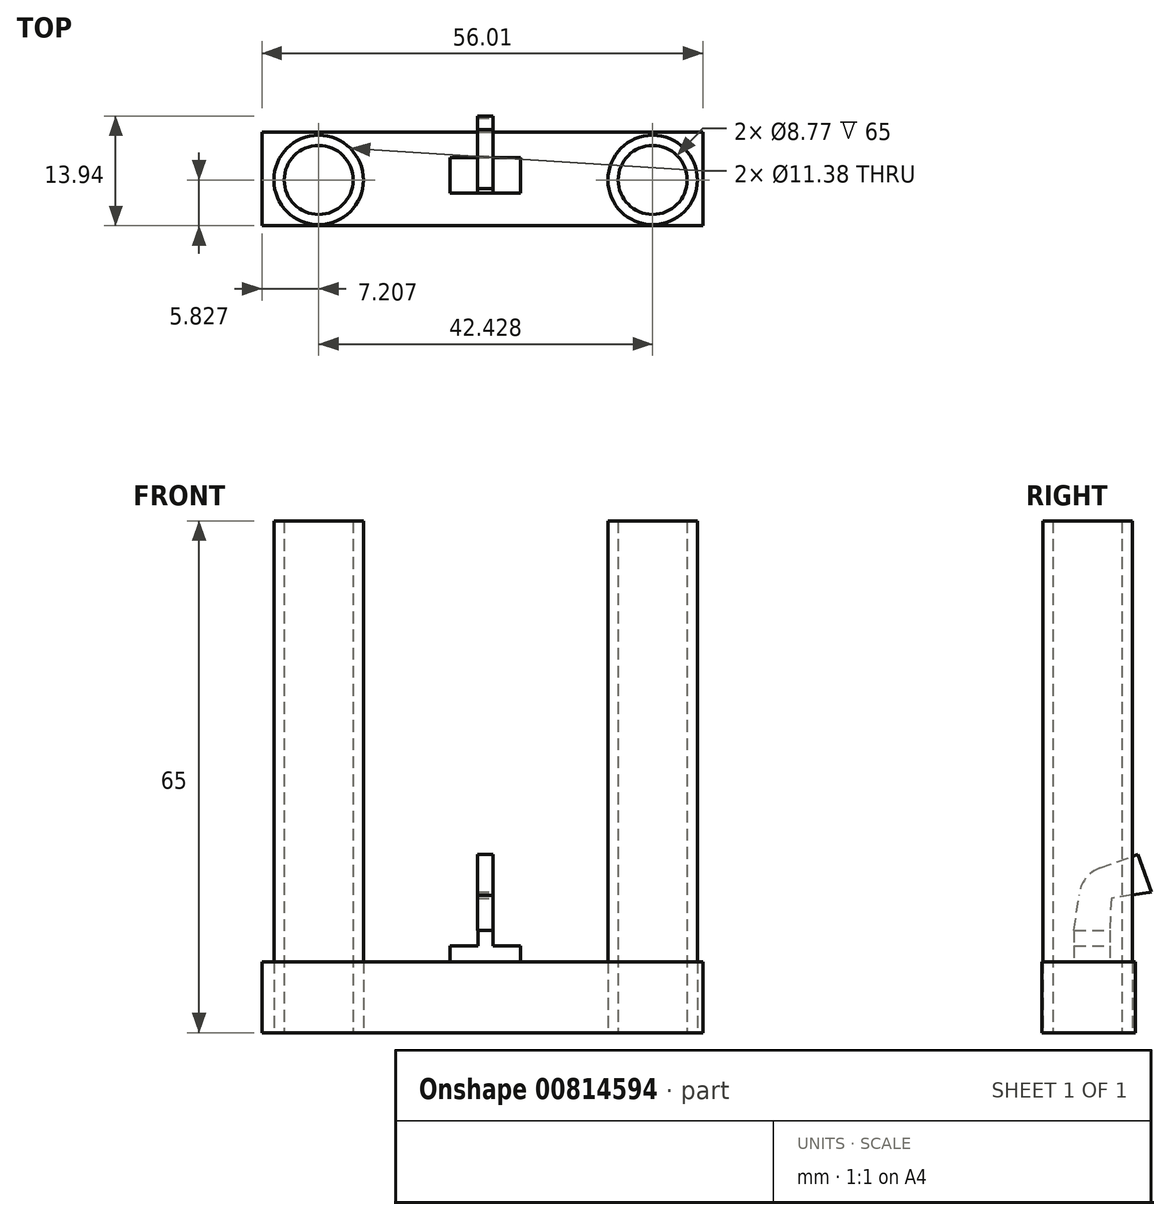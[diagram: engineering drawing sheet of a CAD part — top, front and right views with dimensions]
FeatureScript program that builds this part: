
annotation { "Feature Type Name" : "Feature", "Feature Type Description" : "" }
export const myFeature = defineFeature(function(context is Context, id is Id, definition is map)
    precondition{}
    {
        {
            var Q0;
            Q0=qCreatedBy(makeId("Top.planeOp"),FACE);
            var sketch = newSketch(context, id + "F0", { "sketchPlane" : qUnion([Q0])});
            skCircle(sketch, "E0", {"center": v(21.22, 38.57) * mm, "radius": 5.69 * mm});
            skCircle(sketch, "E1", {"center": v(-21.21, 38.57) * mm, "radius": 5.69 * mm});
            skLineSegment(sketch, "E2.bottom", {"start": v(-28.42, 44.67) * mm, "end": v(27.6, 44.67) * mm});
            skLineSegment(sketch, "E2.top", {"start": v(-28.42, 32.74) * mm, "end": v(27.6, 32.74) * mm});
            skLineSegment(sketch, "E2.left", {"start": v(-28.42, 44.67) * mm, "end": v(-28.42, 32.74) * mm});
            skLineSegment(sketch, "E2.right", {"start": v(27.6, 44.67) * mm, "end": v(27.6, 32.74) * mm});
            skCircle(sketch, "E3", {"center": v(-21.21, 38.57) * mm, "radius": 4.38 * mm});
            skCircle(sketch, "E4", {"center": v(21.22, 38.57) * mm, "radius": 4.38 * mm});
            skSolve(sketch);
        }
        {
            var Q0;
            Q0=makeQuery(id+"F0.imprint","IMPRINT",FACE,{"disambiguationData":[TD([[makeQuery(id+"F0.imprint","IMPRINT",EDGE,{"derivedFrom":sQuery(id+"F0.wireOp",EDGE,"E1")}),1.0]])]});
            var Q1;
            Q1=makeQuery(id+"F0.imprint","IMPRINT",FACE,{"disambiguationData":[TD([[makeQuery(id+"F0.imprint","IMPRINT",EDGE,{"derivedFrom":sQuery(id+"F0.wireOp",EDGE,"E0")}),1.0]])]});
            extrude(context, id + "F1", {"entities" : qUnion([Q0, Q1]), "depth" : 65 * mm, "offsetDistance" : 25 * mm});
        }
        {
            var Q0;
            Q0 = qSketchRegion(id + "F0", true);
            extrude(context, id + "F2", {"entities" : qUnion([Q0]), "depth" : 9 * mm, "offsetDistance" : 25 * mm});
        }
        {
            var Q0;
            Q0=makeQuery(id+"F2.opExtrude","CAP_FACE",FACE,{"disambiguationData":[OSD([sQuery(id+"F0.wireOp",EDGE,"E0"),sQuery(id+"F0.wireOp",EDGE,"E1"),sQuery(id+"F0.wireOp",EDGE,"E2.bottom"),sQuery(id+"F0.wireOp",EDGE,"E2.top"),sQuery(id+"F0.wireOp",EDGE,"E2.left"),sQuery(id+"F0.wireOp",EDGE,"E2.right")])],"isStart":false});
            var sketch = newSketch(context, id + "F3", { "sketchPlane" : qUnion([Q0])});
            skLineSegment(sketch, "E5.bottom", {"start": v(4.46, 36.86) * mm, "end": v(-4.54, 36.86) * mm});
            skLineSegment(sketch, "E5.top", {"start": v(4.46, 41.38) * mm, "end": v(-4.54, 41.38) * mm});
            skLineSegment(sketch, "E5.left", {"start": v(4.46, 36.86) * mm, "end": v(4.46, 41.38) * mm});
            skLineSegment(sketch, "E5.right", {"start": v(-4.54, 36.86) * mm, "end": v(-4.54, 41.38) * mm});
            skSolve(sketch);
        }
        {
            var Q0;
            Q0=makeQuery(id+"F3.imprint","IMPRINT",FACE,{"disambiguationData":[TD([[makeQuery(id+"F3.imprint","IMPRINT",EDGE,{"derivedFrom":sQuery(id+"F3.wireOp",EDGE,"E5.bottom")}),-1.0]])]});
            extrude(context, id + "F4", {"entities" : qUnion([Q0]), "operationType" : NewBodyOperationType.ADD, "depth" : 2 * mm, "offsetDistance" : 25 * mm});
        }
        {
            var Q0;
            Q0=makeQuery(id+"F4.opExtrude","CAP_FACE",FACE,{"disambiguationData":[OSD([sQuery(id+"F3.wireOp",EDGE,"E5.bottom"),sQuery(id+"F3.wireOp",EDGE,"E5.top"),sQuery(id+"F3.wireOp",EDGE,"E5.left"),sQuery(id+"F3.wireOp",EDGE,"E5.right")])],"isStart":false});
            var sketch = newSketch(context, id + "F5", { "sketchPlane" : qUnion([Q0])});
            skLineSegment(sketch, "E6.bottom", {"start": v(0.95, 36.86) * mm, "end": v(-0.94, 36.86) * mm});
            skLineSegment(sketch, "E6.top", {"start": v(0.95, 41.38) * mm, "end": v(-0.94, 41.38) * mm});
            skLineSegment(sketch, "E6.left", {"start": v(0.95, 36.86) * mm, "end": v(0.95, 41.38) * mm});
            skLineSegment(sketch, "E6.right", {"start": v(-0.94, 36.86) * mm, "end": v(-0.94, 41.38) * mm});
            skSolve(sketch);
        }
        {
            var Q0;
            Q0 = qSketchRegion(id + "F5", true);
            var Q1;
            Q1=makeQuery(id+"F5.imprint","IMPRINT",FACE,{"disambiguationData":[TD([[makeQuery(id+"F5.imprint","IMPRINT",EDGE,{"derivedFrom":sQuery(id+"F5.wireOp",EDGE,"E6.bottom")}),-1.0]])]});
            extrude(context, id + "F6", {"entities" : qUnion([Q0, Q1]), "operationType" : NewBodyOperationType.ADD, "depth" : 2 * mm, "offsetDistance" : 25 * mm});
        }
        {
            var Q0;
            Q0=makeQuery(id+"F6.opExtrude","SWEPT_FACE",FACE,{"disambiguationData":[OSD([sQuery(id+"F5.wireOp",EDGE,"E6.left")])]});
            var sketch = newSketch(context, id + "F7", { "sketchPlane" : qUnion([Q0])});
            skLineSegment(sketch, "E7", {"start": v(36.86, 13) * mm, "end": v(37.47, 17.46) * mm});
            skLineSegment(sketch, "E8", {"start": v(40.16, 20.93) * mm, "end": v(44.95, 22.67) * mm});
            skLineSegment(sketch, "E9", {"start": v(44.95, 22.67) * mm, "end": v(46.68, 17.91) * mm});
            skLineSegment(sketch, "E10", {"start": v(46.68, 17.91) * mm, "end": v(46.45, 17.83) * mm});
            skLineSegment(sketch, "E11", {"start": v(46.45, 17.83) * mm, "end": v(41.57, 17.06) * mm});
            skLineSegment(sketch, "E12", {"start": v(41.57, 17.06) * mm, "end": v(41.38, 13) * mm});
            skArc(sketch, "E13", {"start": v(40.16, 20.93) * mm, "mid": v(38.32, 19.58) * mm, "end": v(37.47, 17.46) * mm});
            skSolve(sketch);
        }
        {
            var Q0;
            Q0=makeQuery(id+"F7.imprint","IMPRINT",FACE,{"disambiguationData":[TD([[makeQuery(id+"F7.imprint","IMPRINT",EDGE,{"derivedFrom":sQuery(id+"F7.wireOp",EDGE,"E7")}),-1.0]])]});
            extrude(context, id + "F8", {"entities" : qUnion([Q0]), "oppositeDirection" : true, "depth" : 2 * mm, "offsetDistance" : 25 * mm});
        }
    });
